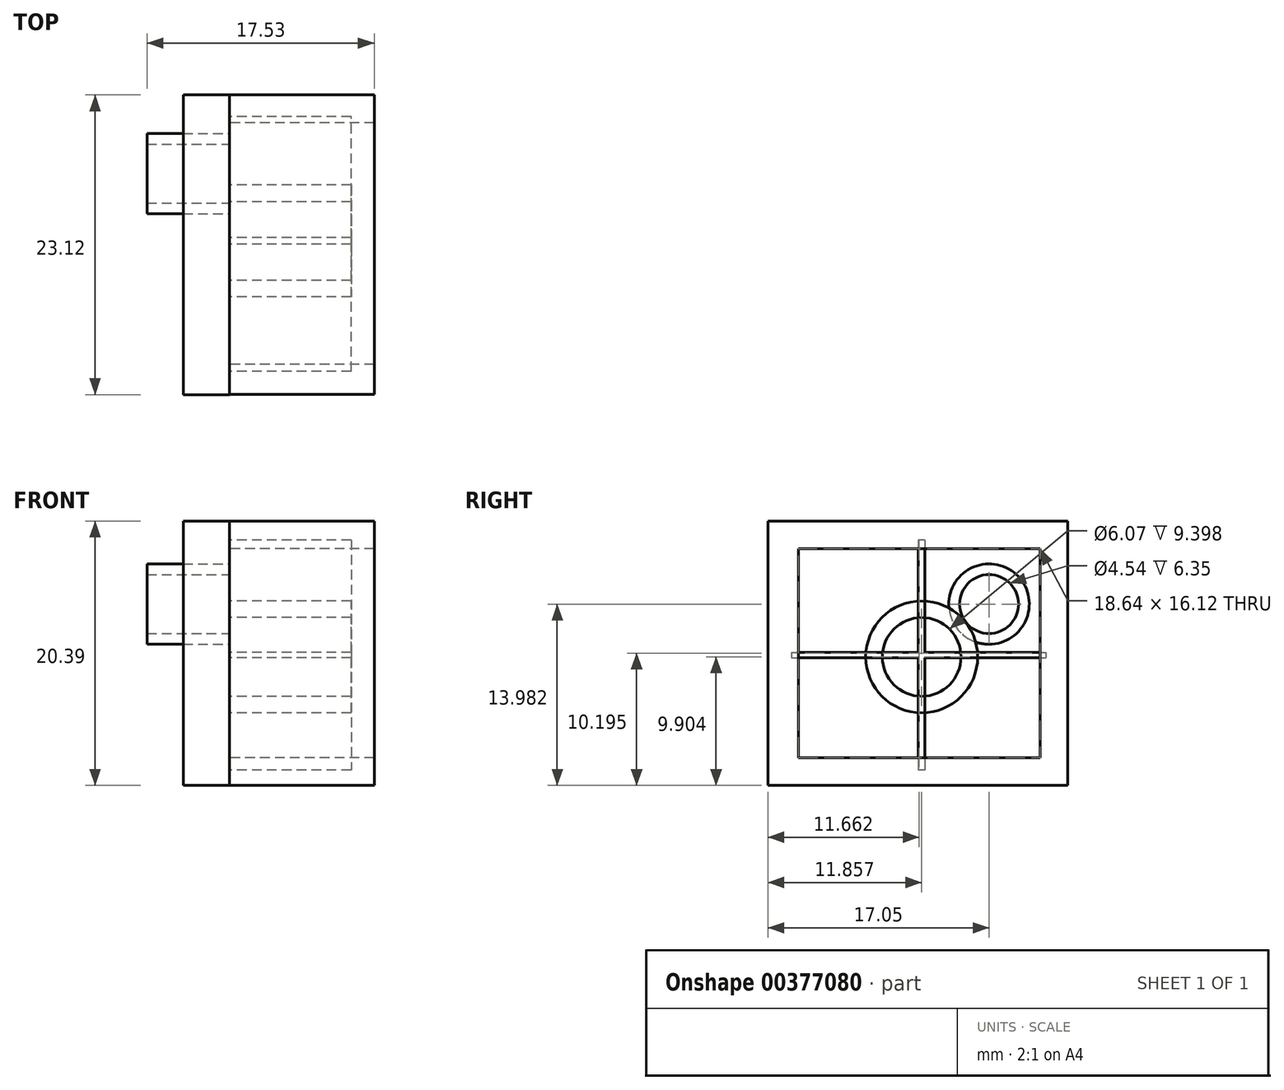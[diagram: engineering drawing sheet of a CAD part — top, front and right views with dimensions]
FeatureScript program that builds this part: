
annotation { "Feature Type Name" : "Feature", "Feature Type Description" : "" }
export const myFeature = defineFeature(function(context is Context, id is Id, definition is map)
    precondition{}
    {
        {
            var Q0;
            Q0=qCreatedBy(makeId("Right.planeOp"),FACE);
            var sketch = newSketch(context, id + "F0", { "sketchPlane" : qUnion([Q0])});
            skLineSegment(sketch, "E0.bottom", {"start": v(0, 0) * mm, "end": v(-23.1, 0) * mm});
            skLineSegment(sketch, "E0.top", {"start": v(0, 20.4) * mm, "end": v(-23.1, 20.4) * mm});
            skLineSegment(sketch, "E0.left", {"start": v(0, 0) * mm, "end": v(0, 20.4) * mm});
            skLineSegment(sketch, "E0.right", {"start": v(-23.1, 0) * mm, "end": v(-23.1, 20.4) * mm});
            skLineSegment(sketch, "E1.bottom", {"start": v(-20.78, 18.25) * mm, "end": v(-2.14, 18.25) * mm});
            skLineSegment(sketch, "E1.top", {"start": v(-20.78, 2.14) * mm, "end": v(-2.14, 2.14) * mm});
            skLineSegment(sketch, "E1.left", {"start": v(-20.78, 18.25) * mm, "end": v(-20.78, 2.14) * mm});
            skLineSegment(sketch, "E1.right", {"start": v(-2.14, 18.25) * mm, "end": v(-2.14, 2.14) * mm});
            skSolve(sketch);
        }
        {
            var Q0;
            Q0 = qSketchRegion(id + "F0", true);
            extrude(context, id + "F1", {"entities" : qUnion([Q0]), "depth" : 11.18 * mm});
        }
        {
            var Q0;
            Q0=qCreatedBy(makeId("Right.planeOp"),FACE);
            var sketch = newSketch(context, id + "F2", { "sketchPlane" : qUnion([Q0])});
            skCircle(sketch, "E2", {"center": v(-11.26, 9.9) * mm, "radius": 4.31 * mm});
            skCircle(sketch, "E3", {"center": v(-11.26, 9.9) * mm, "radius": 3.03 * mm});
            skSolve(sketch);
        }
        {
            var Q0;
            Q0 = qSketchRegion(id + "F2", true);
            extrude(context, id + "F3", {"entities" : qUnion([Q0]), "depth" : 9.4 * mm});
        }
        {
            var Q0;
            Q0=qCreatedBy(makeId("Right.planeOp"),FACE);
            var sketch = newSketch(context, id + "F4", { "sketchPlane" : qUnion([Q0])});
            skLineSegment(sketch, "E4.bottom", {"start": v(-11.02, 18.92) * mm, "end": v(-11.53, 18.92) * mm});
            skLineSegment(sketch, "E4.top", {"start": v(-11.02, 1.17) * mm, "end": v(-11.53, 1.17) * mm});
            skLineSegment(sketch, "E4.left", {"start": v(-11.02, 18.92) * mm, "end": v(-11.02, 1.17) * mm});
            skLineSegment(sketch, "E4.right", {"start": v(-11.53, 18.92) * mm, "end": v(-11.53, 1.17) * mm});
            skPoint(sketch, "E4.middle", {"position": v(-11.27, 10.04) * mm});
            skLineSegment(sketch, "E5.left", {"start": v(0, 10.04) * mm, "end": v(0, 10.04) * mm});
            skLineSegment(sketch, "E5.right", {"start": v(-22.54, 10.04) * mm, "end": v(-22.54, 10.04) * mm});
            skPoint(sketch, "E5.cornerSnap0", {"position": v(-11.02, 10.04) * mm});
            skLineSegment(sketch, "E6.bottom", {"start": v(-21.32, 10.25) * mm, "end": v(-1.68, 10.25) * mm});
            skLineSegment(sketch, "E6.top", {"start": v(-21.32, 9.84) * mm, "end": v(-1.68, 9.84) * mm});
            skLineSegment(sketch, "E6.left", {"start": v(-21.32, 10.25) * mm, "end": v(-21.32, 9.84) * mm});
            skLineSegment(sketch, "E6.right", {"start": v(-1.68, 10.25) * mm, "end": v(-1.68, 9.84) * mm});
            skSolve(sketch);
        }
        {
            var Q0;
            Q0 = qSketchRegion(id + "F4", true);
            extrude(context, id + "F5", {"entities" : qUnion([Q0]), "depth" : 9.4 * mm});
        }
        {
            var Q0;
            Q0=qCreatedBy(makeId("Right.planeOp"),FACE);
            var sketch = newSketch(context, id + "F6", { "sketchPlane" : qUnion([Q0])});
            skLineSegment(sketch, "E7.bottom", {"start": v(-23.12, 20.39) * mm, "end": v(0, 20.39) * mm});
            skLineSegment(sketch, "E7.top", {"start": v(-23.12, 0) * mm, "end": v(0, 0) * mm});
            skLineSegment(sketch, "E7.left", {"start": v(-23.12, 20.39) * mm, "end": v(-23.12, 0) * mm});
            skLineSegment(sketch, "E7.right", {"start": v(0, 20.39) * mm, "end": v(0, 0) * mm});
            skSolve(sketch);
        }
        {
            var Q0;
            Q0 = qSketchRegion(id + "F6", true);
            extrude(context, id + "F7", {"entities" : qUnion([Q0]), "oppositeDirection" : true, "depth" : 3.56 * mm});
        }
        {
            var Q0;
            Q0=qCreatedBy(makeId("Right.planeOp"),FACE);
            var sketch = newSketch(context, id + "F8", { "sketchPlane" : qUnion([Q0])});
            skCircle(sketch, "E8", {"center": v(-6.07, 13.98) * mm, "radius": 3.1 * mm});
            skCircle(sketch, "E9", {"center": v(-6.07, 13.98) * mm, "radius": 2.27 * mm});
            skSolve(sketch);
        }
        {
            var Q0;
            Q0 = qSketchRegion(id + "F8", true);
            extrude(context, id + "F9", {"entities" : qUnion([Q0]), "oppositeDirection" : true, "depth" : 6.35 * mm});
        }
    });
